# Revit family: Diverter_Valve_Trim-American_Standard-Fluent-T186430_Series
name_source: partatom
category: Plumbing Fixtures
units: mm (PartAtom-declared; Revit-internal decimal feet)

## family parameters
Cut with Voids When Loaded = No
Host = Face
OmniClass Number = 23.45.05.14.17
OmniClass Title = Showers
Part Type = Normal
Room Calculation Point = No
Round Connector Dimension = Use Diameter
Shared = Yes

## types (2) — shared parameters
ADA Compliant = Yes
Assembly Code = D2020300
CW Connection = No
CWFU = 3
Compliance Certifications = ASME A112.18.1 and ANSI A117.1
Connection Description = 1/2'' NPT Supply Outlet 3
Default Elevation = 48"
Description = Fluent® Single-Handle Diverter Valve Trim Kit
HW Connection = No
HWFU = 3
Height = 3 7/8"
Installation Type = Wall Mounted
Length = 3 7/8"
Manufacturer = American Standard
Price = Prices may vary. Please consult Manufacturer Representative for most up-to-date price list.
Product Documentation Link = https://americanstandard.box.com
Product Page URL = https://www.americanstandard-us.com
R422 Two-Way In-Wall Diverter Valve Rough (Discrete) = No
R422S Two-Way In-Wall Diverter Valve Rough (Shared) = No
R433 Three-Way In-Wall Diverter Valve Rough (Discrete) = No
R433S Three-Way In-Wall Diverter Valve Rough (Shared) = No
Revised Date = 08/02/2022
Tempered Water Connection = Yes
Tempered Water Connection Diameter = 1/2"
Third Connection = 1/2"
Trim Constraint = 1 5/8"
Trim Distance from Wall (min. 1 5/8- 2 5/8") = 1 5/8"
URL = https://www.americanstandard-us.com
Vent Connection = No
WFU = 4
Warranty Information = Limited Lifetime Function and Finish Warranty
Waste Connection = No
Width = 1 15/16"

## per-type parameters (varying)
| type | Finish | Material |
| T186.430.002 | Solid Brass-American Standard-002-Polished Chrome | Solid Brass-American Standard-002-Polished Chrome |
| T186.430.295 | Solid Brass-American Standard-295-Brushed Nickel | Solid Brass-American Standard-295-Brushed Nickel |

note: column(s) folded — value = type name in every type: Model

## geometry (parser evidence)
native form markers: Sweep x3
no freeform markers — native parametric forms only
